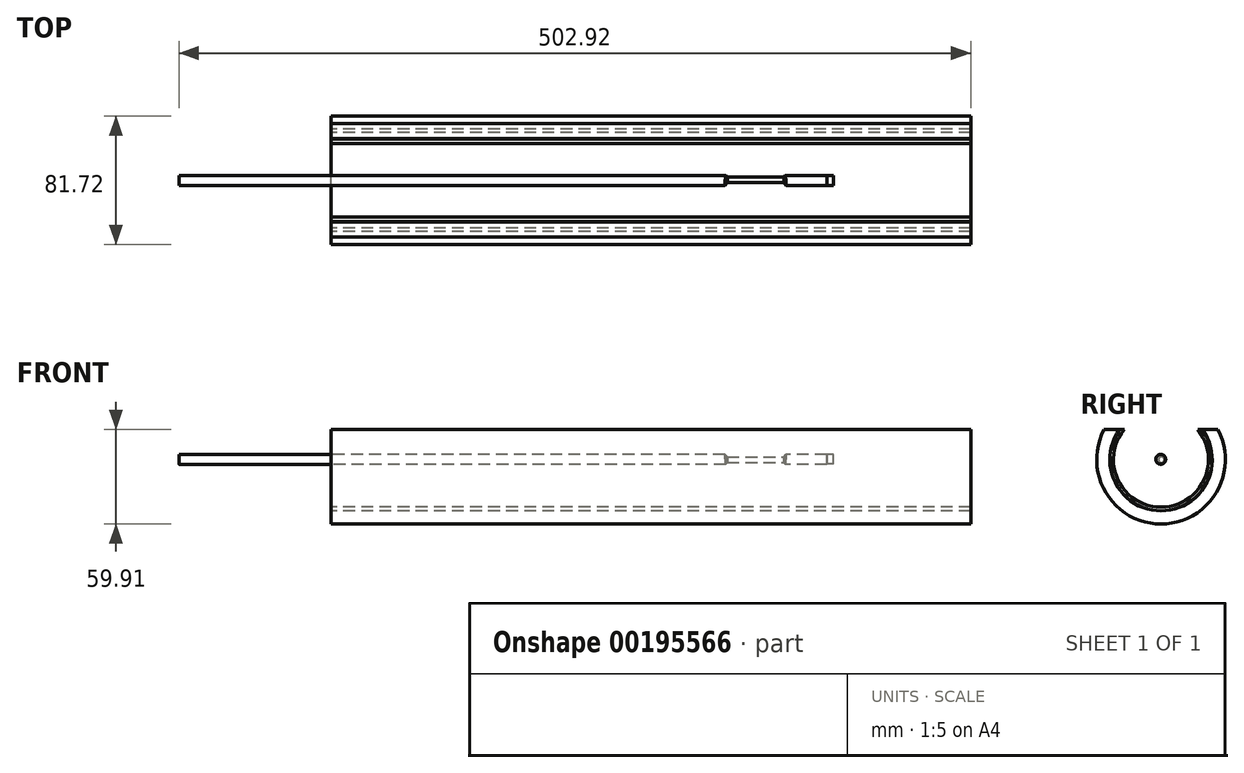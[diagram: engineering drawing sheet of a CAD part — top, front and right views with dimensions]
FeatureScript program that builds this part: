
annotation { "Feature Type Name" : "Feature", "Feature Type Description" : "" }
export const myFeature = defineFeature(function(context is Context, id is Id, definition is map)
    precondition{}
    {
        {
            var Q0;
            Q0=qCreatedBy(makeId("Right.planeOp"),FACE);
            var sketch = newSketch(context, id + "F0", { "sketchPlane" : qUnion([Q0])});
            skCircle(sketch, "E0", {"center": v(0, 0) * mm, "radius": 32.47 * mm});
            skCircle(sketch, "E1", {"center": v(0, 0) * mm, "radius": 30.17 * mm});
            skSolve(sketch);
        }
        {
            var Q0;
            Q0 = qSketchRegion(id + "F0", true);
            extrude(context, id + "F1", {"entities" : qUnion([Q0]), "depth" : 203.2 * mm, "hasSecondDirection" : true, "secondDirectionOppositeDirection" : true, "secondDirectionDepth" : 203.2 * mm});
        }
        {
            var Q0;
            Q0=qCreatedBy(makeId("Right.planeOp"),FACE);
            var sketch = newSketch(context, id + "F2", { "sketchPlane" : qUnion([Q0])});
            skCircle(sketch, "E2", {"center": v(0, 0) * mm, "radius": 32.56 * mm});
            skCircle(sketch, "E3", {"center": v(0, 0) * mm, "radius": 40.86 * mm});
            skSolve(sketch);
        }
        {
            var Q0;
            Q0 = qSketchRegion(id + "F2", true);
            extrude(context, id + "F3", {"entities" : qUnion([Q0]), "depth" : 203.2 * mm, "hasSecondDirection" : true, "secondDirectionOppositeDirection" : true, "secondDirectionDepth" : 203.2 * mm});
        }
        {
            var Q0;
            Q0=qCreatedBy(makeId("Right.planeOp"),FACE);
            var sketch = newSketch(context, id + "F4", { "sketchPlane" : qUnion([Q0])});
            skCircle(sketch, "E4", {"center": v(-0.15, 0.19) * mm, "radius": 3.15 * mm});
            skSolve(sketch);
        }
        {
            var Q0;
            Q0 = qSketchRegion(id + "F4", true);
            extrude(context, id + "F5", {"entities" : qUnion([Q0]), "depth" : 111.76 * mm, "hasSecondDirection" : true, "secondDirectionOppositeDirection" : true, "secondDirectionDepth" : 299.72 * mm});
        }
        {
            var Q0;
            Q0=qCreatedBy(makeId("Top.planeOp"),FACE);
            var sketch = newSketch(context, id + "F6", { "sketchPlane" : qUnion([Q0])});
            skLineSegment(sketch, "E5", {"start": v(48.63, 2.08) * mm, "end": v(46.16, 4.73) * mm});
            skLineSegment(sketch, "E6", {"start": v(46.16, 4.73) * mm, "end": v(86.78, 4.73) * mm});
            skLineSegment(sketch, "E7", {"start": v(86.78, 4.73) * mm, "end": v(84.48, 2.08) * mm});
            skLineSegment(sketch, "E8", {"start": v(84.48, 2.08) * mm, "end": v(48.63, 2.08) * mm});
            skSolve(sketch);
        }
        {
            var Q0;
            Q0=qCreatedBy(makeId("Top.planeOp"),FACE);
            var sketch = newSketch(context, id + "F7", { "sketchPlane" : qUnion([Q0])});
            skLineSegment(sketch, "E9", {"start": v(-75.89, 0.27) * mm, "end": v(131.98, 0.27) * mm});
            skSolve(sketch);
        }
        {
            var Q0;
            Q0 = qSketchRegion(id + "F6", true);
            var Q1;
            Q1=sQuery(id+"F7.wireOp",EDGE,"E9");
            revolve(context, id + "F8", {"operationType" : NewBodyOperationType.REMOVE, "entities" : qUnion([Q0]), "axis" : qUnion([Q1]), "revolveType" : RevolveType.FULL, "oppositeDirection" : true});
        }
        {
            var Q0;
            Q0=qCreatedBy(makeId("Right.planeOp"),FACE);
            cPlane(context, id + "F9", {"entities" : qUnion([Q0]), "cplaneType" : CPlaneType.OFFSET, "offset" : 111.76 * mm, "width" : 152.4 * mm, "height" : 152.4 * mm});
        }
        {
            var Q0;
            Q0=qCreatedBy(id+"F9.planeOp",FACE);
            var sketch = newSketch(context, id + "F10", { "sketchPlane" : qUnion([Q0])});
            skCircle(sketch, "E10", {"center": v(-0.11, 0.19) * mm, "radius": 3.07 * mm});
            skSolve(sketch);
        }
        {
            var Q0;
            Q0 = qSketchRegion(id + "F10", true);
            extrude(context, id + "F11", {"entities" : qUnion([Q0]), "depth" : 4.32 * mm});
        }
        {
            var Q0;
            Q0=qCreatedBy(makeId("Top.planeOp"),FACE);
            cPlane(context, id + "F12", {"entities" : qUnion([Q0]), "cplaneType" : CPlaneType.OFFSET, "offset" : 19.05 * mm, "width" : 152.4 * mm, "height" : 152.4 * mm});
        }
        {
            var Q0;
            Q0=qCreatedBy(id+"F12.planeOp",FACE);
            var sketch = newSketch(context, id + "F13", { "sketchPlane" : qUnion([Q0])});
            skLineSegment(sketch, "E11.bottom", {"start": v(-214.92, 45.6) * mm, "end": v(211.11, 45.6) * mm});
            skLineSegment(sketch, "E11.top", {"start": v(-214.92, -47.34) * mm, "end": v(211.11, -47.34) * mm});
            skLineSegment(sketch, "E11.left", {"start": v(-214.92, 45.6) * mm, "end": v(-214.92, -47.34) * mm});
            skLineSegment(sketch, "E11.right", {"start": v(211.11, 45.6) * mm, "end": v(211.11, -47.34) * mm});
            skSolve(sketch);
        }
        {
            var Q0;
            Q0 = qSketchRegion(id + "F13", true);
            extrude(context, id + "F14", {"entities" : qUnion([Q0]), "operationType" : NewBodyOperationType.REMOVE, "depth" : 35.81 * mm});
        }
    });
